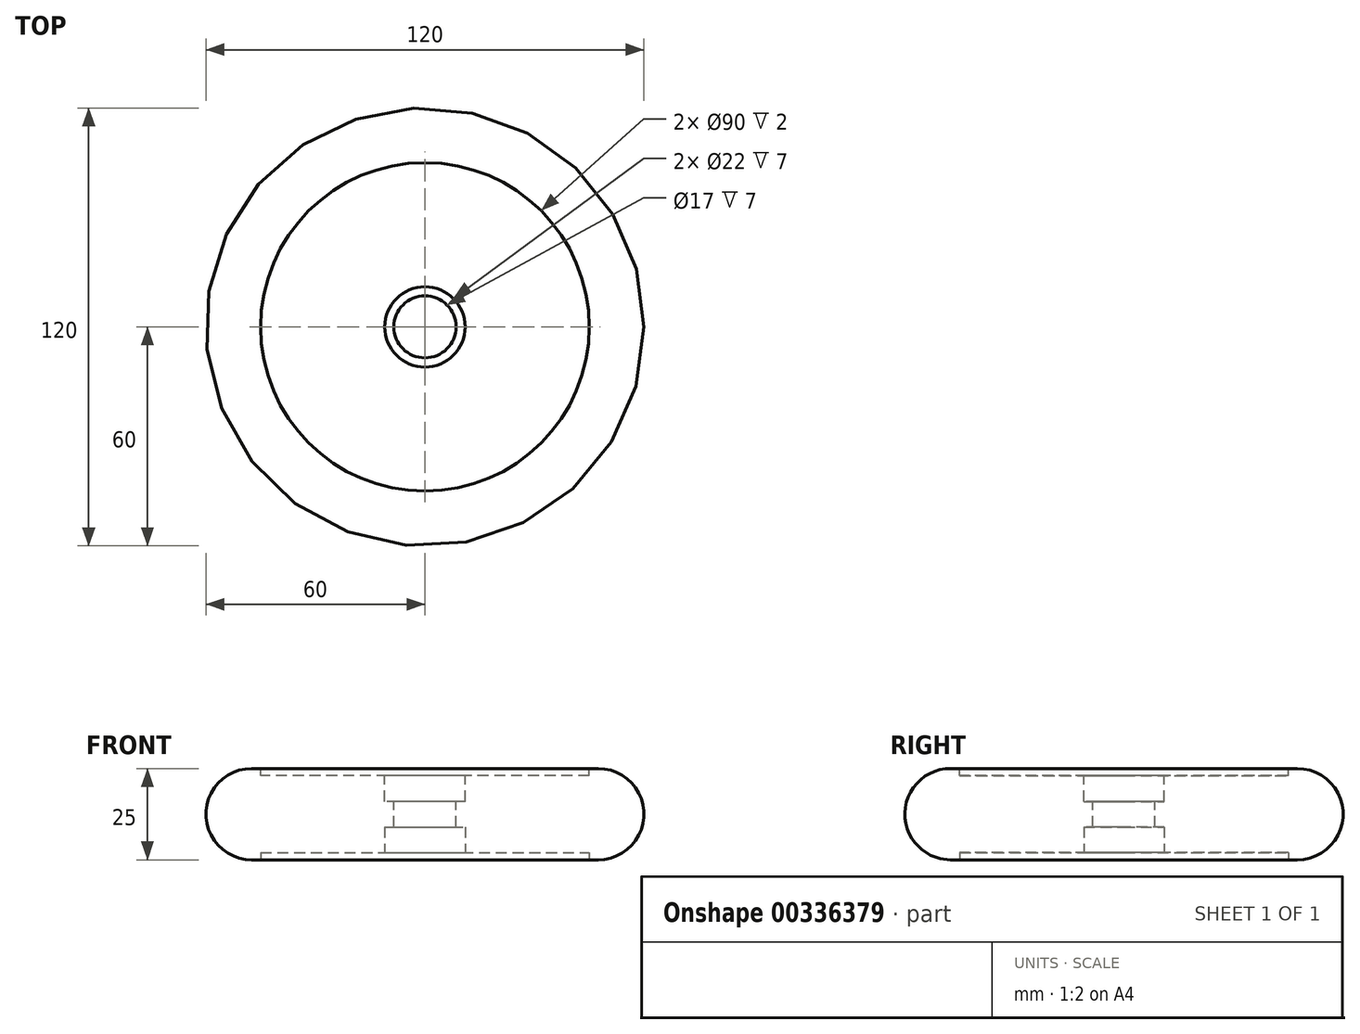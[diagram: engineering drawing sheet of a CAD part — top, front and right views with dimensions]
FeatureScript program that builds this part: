
annotation { "Feature Type Name" : "Feature", "Feature Type Description" : "" }
export const myFeature = defineFeature(function(context is Context, id is Id, definition is map)
    precondition{}
    {
        {
            var Q0;
            Q0=qCreatedBy(makeId("Top.planeOp"),FACE);
            var sketch = newSketch(context, id + "F0", { "sketchPlane" : qUnion([Q0])});
            skCircle(sketch, "E0", {"center": v(0, 0) * mm, "radius": 60 * mm});
            skSolve(sketch);
        }
        {
            var Q0;
            Q0=makeQuery(id+"F0.imprint","IMPRINT",FACE,{"disambiguationData":[TD([[makeQuery(id+"F0.imprint","IMPRINT",EDGE,{"derivedFrom":sQuery(id+"F0.wireOp",EDGE,"E0")}),1.0]])]});
            extrude(context, id + "F1", {"entities" : qUnion([Q0]), "depth" : 25 * mm});
        }
        {
            var Q0;
            Q0=makeQuery(id+"F1.opExtrude","CAP_FACE",FACE,{"disambiguationData":[OSD([sQuery(id+"F0.wireOp",EDGE,"E0")])],"isStart":false});
            var sketch = newSketch(context, id + "F2", { "sketchPlane" : qUnion([Q0])});
            skCircle(sketch, "E1", {"center": v(0, 0) * mm, "radius": 11 * mm});
            skSolve(sketch);
        }
        {
            var Q0;
            Q0=makeQuery(id+"F2.imprint","IMPRINT",FACE,{"disambiguationData":[TD([[makeQuery(id+"F2.imprint","IMPRINT",EDGE,{"derivedFrom":sQuery(id+"F2.wireOp",EDGE,"E1")}),-1.0]])]});
            var sketch = newSketch(context, id + "F3", { "sketchPlane" : qUnion([Q0])});
            skCircle(sketch, "E2", {"center": v(0, 0) * mm, "radius": 45 * mm});
            skSolve(sketch);
        }
        {
            var Q0;
            Q0 = qSketchRegion(id + "F2", true);
            extrude(context, id + "F4", {"entities" : qUnion([Q0]), "operationType" : NewBodyOperationType.REMOVE, "oppositeDirection" : true, "depth" : 9 * mm});
        }
        {
            var Q0;
            Q0=makeQuery(id+"F3.imprint","IMPRINT",FACE,{"disambiguationData":[TD([[makeQuery(id+"F3.imprint","IMPRINT",EDGE,{"derivedFrom":sQuery(id+"F3.wireOp",EDGE,"E2")}),1.0]])]});
            extrude(context, id + "F5", {"entities" : qUnion([Q0]), "operationType" : NewBodyOperationType.REMOVE, "oppositeDirection" : true, "depth" : 0.01 * mm});
        }
        {
            var Q0;
            Q0 = qSketchRegion(id + "F3", true);
            extrude(context, id + "F6", {"entities" : qUnion([Q0]), "operationType" : NewBodyOperationType.REMOVE, "oppositeDirection" : true, "depth" : 2 * mm});
        }
        {
            var Q0;
            Q0=makeQuery(id+"F1.opExtrude","CAP_FACE",FACE,{"disambiguationData":[OSD([sQuery(id+"F0.wireOp",EDGE,"E0")])],"isStart":true});
            var sketch = newSketch(context, id + "F7", { "sketchPlane" : qUnion([Q0])});
            skCircle(sketch, "E3", {"center": v(0, 0) * mm, "radius": 11 * mm});
            skSolve(sketch);
        }
        {
            var Q0;
            Q0=makeQuery(id+"F7.imprint","IMPRINT",FACE,{"disambiguationData":[TD([[makeQuery(id+"F7.imprint","IMPRINT",EDGE,{"derivedFrom":sQuery(id+"F7.wireOp",EDGE,"E3")}),-1.0]])]});
            var sketch = newSketch(context, id + "F8", { "sketchPlane" : qUnion([Q0])});
            skCircle(sketch, "E4", {"center": v(0, 0) * mm, "radius": 45 * mm});
            skSolve(sketch);
        }
        {
            var Q0;
            Q0 = qSketchRegion(id + "F7", true);
            extrude(context, id + "F9", {"entities" : qUnion([Q0]), "operationType" : NewBodyOperationType.REMOVE, "oppositeDirection" : true, "depth" : 9 * mm});
        }
        {
            var Q0;
            Q0 = qSketchRegion(id + "F8", true);
            extrude(context, id + "F10", {"entities" : qUnion([Q0]), "operationType" : NewBodyOperationType.REMOVE, "oppositeDirection" : true, "depth" : 2 * mm});
        }
        {
            var Q0;
            Q0=makeQuery(id+"F1.opExtrude","CAP_EDGE",EDGE,{"disambiguationData":[OSD([sQuery(id+"F0.wireOp",EDGE,"E0")])],"isStart":false});
            fillet(context, id + "F11", {"entities" : qUnion([Q0]), "radius" : 12.5 * mm, "tangentPropagation" : true, "allowEdgeOverflow" : false});
        }
        {
            var Q0;
            Q0=makeQuery(id+"F1.opExtrude","CAP_EDGE",EDGE,{"disambiguationData":[OSD([sQuery(id+"F0.wireOp",EDGE,"E0")])],"isStart":true});
            fillet(context, id + "F12", {"entities" : qUnion([Q0]), "radius" : 12.5 * mm, "tangentPropagation" : true, "allowEdgeOverflow" : false});
        }
        {
            var Q0;
            Q0=makeQuery(id+"F4.boolean.opBoolean","COPY",FACE,{"derivedFrom":makeQuery(id+"F4.opExtrude","CAP_FACE",FACE,{"disambiguationData":[OSD([sQuery(id+"F2.wireOp",EDGE,"E1")])],"isStart":false})});
            var sketch = newSketch(context, id + "F13", { "sketchPlane" : qUnion([Q0])});
            skCircle(sketch, "E5", {"center": v(0, 0) * mm, "radius": 8.5 * mm});
            skSolve(sketch);
        }
        {
            var Q0;
            Q0=makeQuery(id+"F13.imprint","IMPRINT",FACE,{"disambiguationData":[TD([[makeQuery(id+"F13.imprint","IMPRINT",EDGE,{"derivedFrom":sQuery(id+"F13.wireOp",EDGE,"E5")}),1.0]])]});
            extrude(context, id + "F14", {"entities" : qUnion([Q0]), "operationType" : NewBodyOperationType.REMOVE, "oppositeDirection" : true, "depth" : 25 * mm});
        }
    });
